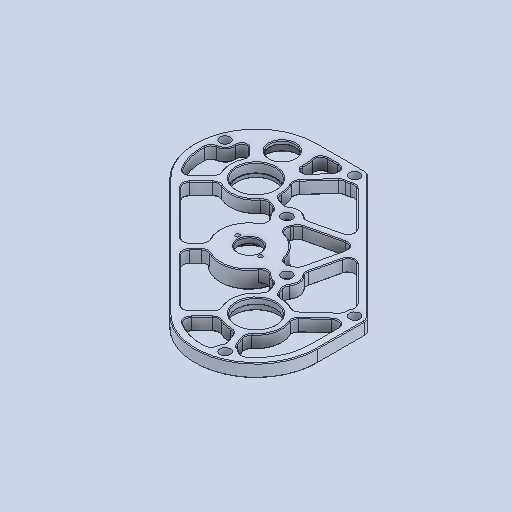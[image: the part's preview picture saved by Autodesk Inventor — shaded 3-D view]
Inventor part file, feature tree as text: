
AUTODESK INVENTOR PART (.ipt)
format: ipt  version: 2023.2 (Build 272271000, 271)  size: 486,400 bytes
history: native  units: in
note: dims shown in document units (in); Inventor stores cm internally (conversion verified against a paired STEP export)
features: chamfer x1
ambient origin geometry x8: Origin, YZ Plane, XZ Plane, XY Plane, X Axis, Y Axis, Z Axis, Center Point
bodies: Solid1 (feature_tree)
feature tree (1):
  chamfer  "Chamfer4"  [1 undecoded]
note: 1 required parameter value undecoded (feature->parameter linkage not recoverable at this tier; creation-order binding heuristic only, values carry confidence <= 0.55)
